# Revit family: Shower-Valve_Trim-KOHLER-Triton-K-T7751_1
name_source: partatom
category: Plumbing Fixtures
revit_build: Autodesk Revit 2017 (Build: 20160225_1515(x64)
units: mm (PartAtom-declared; Revit-internal decimal feet)

## family parameters
Cut with Voids When Loaded = No
Host = Face
OmniClass Number = 23.31.11.00
OmniClass Title = Faucets
Part Type = Normal
Room Calculation Point = No
Round Connector Dimension = Use Diameter
Shared = No

## types (3) — shared parameters
ADA Compliant = No
Assembly Code = D2010
CW Connection = Yes
Cold Water Inlet = Cold Water Inlet
Date Modified = 02/16/2021
Default Elevation = 36"
Drain Included = No
Finish = Kohler-Metal-CP-Polished_Chrome
Flow Rate = 0 GPM
HW Connection = Yes
Hot Water Inlet = Hot Water Inlet
Manufacturer = KOHLER Co.
Master Format 2014 = 22 41 39
Master Format 2014 Name = Residential Faucets, Supplies, and Trim
Material = Brass Construction
Pressure = 0.00 psi
Product Documentation Link = https://www.us.kohler.com
Product Name = Triton
Product Page URL = http://www.us.kohler.com
Spout Reach = 0"
URL = https://www.us.kohler.com
Vent Connection = No
Waste Connection = No
Waste Water Outlet = Waste Water Outlet
WaterSense Certified = No

## per-type parameters (varying)
| type | Description | Handle Clearance | Height | K-T7751-2 | K-T7751-3 | K-T7751-4 | Length | Model | T_F | Type |
| Standard Handles, CP-Polished Chrome | Wall-mount valve trim with push button diverter and standard handles, requires valve | 1 1/4" | 2 1/8" | Yes | No | No | 2 1/2" | K-T7751-2-CP | 12" | 1 |
| Cross Handles, CP-Polished Chrome | Wall-mount valve trim with push button diverter and cross handles, requires valve | 1 7/16" | 2 15/16" | No | Yes | No | 2 7/8" | K-T7751-3-CP | 6" | 2 |
| Lever Handles, CP-Polished Chrome | Wall-mount valve trim with push button diverter and Lever handles, requires valve | 2 7/16" | 2 1/2" | No | No | Yes | 2 1/2" | K-T7751-4-CP | 0" | 3 |

## geometry (parser evidence)
native form markers: Sweep x6
no freeform markers — native parametric forms only
